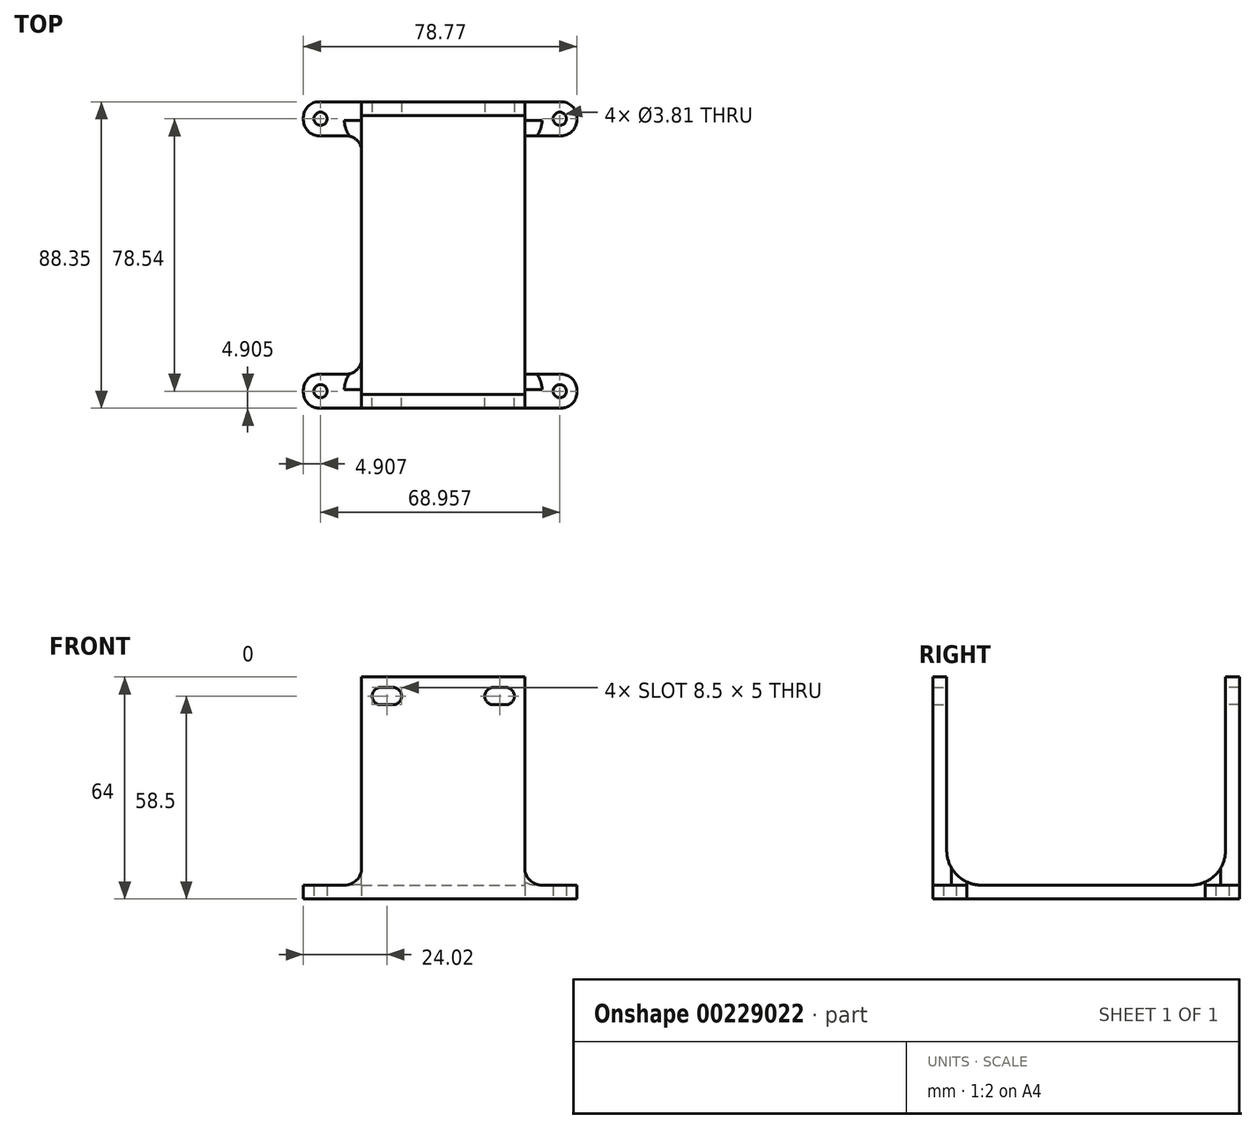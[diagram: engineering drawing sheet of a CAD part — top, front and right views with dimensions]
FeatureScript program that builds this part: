
annotation { "Feature Type Name" : "Feature", "Feature Type Description" : "" }
export const myFeature = defineFeature(function(context is Context, id is Id, definition is map)
    precondition{}
    {
        {
            var Q0;
            Q0=qCreatedBy(makeId("Front.planeOp"),FACE);
            var sketch = newSketch(context, id + "F0", { "sketchPlane" : qUnion([Q0])});
            skLineSegment(sketch, "E0.bottom", {"start": v(0, 0) * mm, "end": v(47, 0) * mm});
            skLineSegment(sketch, "E0.top", {"start": v(0, 64) * mm, "end": v(47, 64) * mm});
            skLineSegment(sketch, "E0.left", {"start": v(0, 0) * mm, "end": v(0, 64) * mm});
            skLineSegment(sketch, "E0.right", {"start": v(47, 0) * mm, "end": v(47, 64) * mm});
            skLineSegment(sketch, "E1", {"start": v(23.5, 64) * mm, "end": v(23.5, 61) * mm, "construction": true});
            skLineSegment(sketch, "E2", {"start": v(23.5, 61) * mm, "end": v(3, 61) * mm, "construction": true});
            skLineSegment(sketch, "E3", {"start": v(3, 61) * mm, "end": v(0, 61) * mm, "construction": true});
            skLineSegment(sketch, "E4", {"start": v(23.5, 61) * mm, "end": v(44, 61) * mm, "construction": true});
            skLineSegment(sketch, "E5", {"start": v(44, 61) * mm, "end": v(47, 61) * mm, "construction": true});
            skLineSegment(sketch, "E6", {"start": v(3, 61) * mm, "end": v(3, 56) * mm, "construction": true});
            skLineSegment(sketch, "E7", {"start": v(44, 61) * mm, "end": v(44, 56) * mm, "construction": true});
            skLineSegment(sketch, "E8", {"start": v(3, 58.5) * mm, "end": v(5.5, 58.5) * mm, "construction": true});
            skLineSegment(sketch, "E9", {"start": v(44, 58.5) * mm, "end": v(41.5, 58.5) * mm, "construction": true});
            skArc(sketch, "E10", {"start": v(5.5, 61) * mm, "mid": v(3, 58.5) * mm, "end": v(5.5, 56) * mm});
            skArc(sketch, "E11", {"start": v(41.5, 61) * mm, "mid": v(44, 58.5) * mm, "end": v(41.5, 56) * mm});
            skLineSegment(sketch, "E12", {"start": v(5.5, 58.5) * mm, "end": v(9, 58.5) * mm, "construction": true});
            skLineSegment(sketch, "E13", {"start": v(41.5, 58.5) * mm, "end": v(38, 58.5) * mm, "construction": true});
            skArc(sketch, "E14", {"start": v(9, 61) * mm, "mid": v(11.5, 58.5) * mm, "end": v(9, 56) * mm});
            skArc(sketch, "E15", {"start": v(38, 61) * mm, "mid": v(35.5, 58.5) * mm, "end": v(38, 56) * mm});
            skLineSegment(sketch, "E16", {"start": v(9, 61) * mm, "end": v(5.5, 61) * mm});
            skLineSegment(sketch, "E17", {"start": v(5.5, 56) * mm, "end": v(9, 56) * mm});
            skLineSegment(sketch, "E18", {"start": v(38, 61) * mm, "end": v(41.5, 61) * mm});
            skLineSegment(sketch, "E19", {"start": v(38, 56) * mm, "end": v(41.5, 56) * mm});
            skSolve(sketch);
        }
        {
            var Q0;
            Q0 = qSketchRegion(id + "F0", true);
            extrude(context, id + "F1", {"entities" : qUnion([Q0]), "depth" : 4 * mm});
        }
        {
            var Q0;
            Q0=makeQuery(id+"F1.opExtrude","SWEPT_FACE",FACE,{"disambiguationData":[OSD([sQuery(id+"F0.wireOp",EDGE,"E0.bottom")])]});
            var sketch = newSketch(context, id + "F2", { "sketchPlane" : qUnion([Q0])});
            skLineSegment(sketch, "E20.bottom", {"start": v(47, 4) * mm, "end": v(0, 4) * mm});
            skLineSegment(sketch, "E20.top", {"start": v(47, -40.18) * mm, "end": v(0, -40.18) * mm});
            skLineSegment(sketch, "E20.left", {"start": v(47, 4) * mm, "end": v(47, -40.18) * mm});
            skLineSegment(sketch, "E20.right", {"start": v(0, 4) * mm, "end": v(0, -40.18) * mm});
            skSolve(sketch);
        }
        {
            var Q0;
            Q0 = qSketchRegion(id + "F2", true);
            extrude(context, id + "F3", {"entities" : qUnion([Q0]), "operationType" : NewBodyOperationType.ADD, "oppositeDirection" : true, "depth" : 4 * mm});
        }
        {
            var Q0;
            Q0=makeQuery(id+"F3.boolean.opBoolean","MERGE",FACE,{"derivedFrom":[makeQuery(id+"F1.opExtrude","SWEPT_FACE",FACE,{"disambiguationData":[OSD([sQuery(id+"F0.wireOp",EDGE,"E0.bottom")])]}),makeQuery(id+"F3.opExtrude","CAP_FACE",FACE,{"disambiguationData":[OSD([sQuery(id+"F2.wireOp",EDGE,"E20.bottom"),sQuery(id+"F2.wireOp",EDGE,"E20.top"),sQuery(id+"F2.wireOp",EDGE,"E20.left"),sQuery(id+"F2.wireOp",EDGE,"E20.right")])],"isStart":true})]});
            var sketch = newSketch(context, id + "F4", { "sketchPlane" : qUnion([Q0])});
            skLineSegment(sketch, "E21.bottom", {"start": v(47, 4) * mm, "end": v(62, 4) * mm});
            skLineSegment(sketch, "E21.top", {"start": v(47, -5.81) * mm, "end": v(62, -5.81) * mm});
            skLineSegment(sketch, "E21.left", {"start": v(47, 4) * mm, "end": v(47, -5.81) * mm});
            skLineSegment(sketch, "E21.right", {"start": v(62, 4) * mm, "end": v(62, -5.81) * mm});
            skCircle(sketch, "E22", {"center": v(57.1, -0.9) * mm, "radius": 1.9 * mm});
            skLineSegment(sketch, "E23", {"start": v(-16.77, 4) * mm, "end": v(-16.77, -5.81) * mm});
            skCircle(sketch, "E24", {"center": v(-11.86, -0.9) * mm, "radius": 1.9 * mm});
            skLineSegment(sketch, "E25", {"start": v(-11.86, -0.9) * mm, "end": v(-11.86, 1) * mm});
            skLineSegment(sketch, "E26", {"start": v(-11.86, 1) * mm, "end": v(-11.86, 4) * mm, "construction": true});
            skLineSegment(sketch, "E27", {"start": v(-11.86, -0.9) * mm, "end": v(-11.86, -2.81) * mm});
            skLineSegment(sketch, "E28", {"start": v(-11.86, -2.81) * mm, "end": v(-11.86, -5.8) * mm, "construction": true});
            skLineSegment(sketch, "E29", {"start": v(-16.77, -5.8) * mm, "end": v(-11.86, -5.8) * mm});
            skLineSegment(sketch, "E30", {"start": v(-11.86, 4) * mm, "end": v(0, 4) * mm});
            skLineSegment(sketch, "E31", {"start": v(-11.86, 4) * mm, "end": v(-16.77, 4) * mm});
            skLineSegment(sketch, "E32", {"start": v(-11.86, -5.8) * mm, "end": v(0.23, -5.8) * mm});
            skLineSegment(sketch, "E33", {"start": v(-16.77, -0.9) * mm, "end": v(-13.77, -0.9) * mm, "construction": true});
            skLineSegment(sketch, "E34", {"start": v(57.1, -0.9) * mm, "end": v(57.1, 1) * mm, "construction": true});
            skLineSegment(sketch, "E35", {"start": v(57.1, 1) * mm, "end": v(57.1, 4) * mm, "construction": true});
            skLineSegment(sketch, "E36", {"start": v(57.1, -0.9) * mm, "end": v(57.1, -2.81) * mm, "construction": true});
            skLineSegment(sketch, "E37", {"start": v(57.1, -2.81) * mm, "end": v(57.1, -5.81) * mm, "construction": true});
            skLineSegment(sketch, "E38", {"start": v(57.1, -0.9) * mm, "end": v(59, -0.9) * mm, "construction": true});
            skLineSegment(sketch, "E39", {"start": v(59, -0.9) * mm, "end": v(62, -0.9) * mm, "construction": true});
            skLineSegment(sketch, "E40", {"start": v(0, 4) * mm, "end": v(1.28, 4) * mm});
            skLineSegment(sketch, "E41", {"start": v(1.28, 3.98) * mm, "end": v(1.28, -5.96) * mm});
            skLineSegment(sketch, "E42", {"start": v(0.23, -5.81) * mm, "end": v(1.28, -5.96) * mm});
            skLineSegment(sketch, "E43", {"start": v(47, 4) * mm, "end": v(45.9, 4) * mm});
            skLineSegment(sketch, "E44", {"start": v(45.9, 3.85) * mm, "end": v(45.9, -5.8) * mm});
            skLineSegment(sketch, "E45", {"start": v(45.9, -5.8) * mm, "end": v(47, -5.81) * mm});
            skSolve(sketch);
        }
        {
            var Q0;
            Q0=makeQuery(id+"F4.imprint","IMPRINT",FACE,{"disambiguationData":[TD([[makeQuery(id+"F4.imprint","IMPRINT",EDGE,{"derivedFrom":sQuery(id+"F4.wireOp",EDGE,"E23")}),1.0]])]});
            var Q1;
            {var subQ6=sQuery(id+"F4.wireOp",EDGE,"E21.left");Q1=makeQuery(id+"F4.imprint","IMPRINT",FACE,{"disambiguationData":[TD([[makeQuery(id+"F4.imprint","IMPRINT",EDGE,{"derivedFrom":subQ6}),-1.0]])]});}
            var Q2;
            Q2=makeQuery(id+"F4.imprint","IMPRINT",FACE,{"disambiguationData":[TD([[makeQuery(id+"F4.imprint","IMPRINT",EDGE,{"derivedFrom":sQuery(id+"F4.wireOp",EDGE,"E21.bottom")}),-1.0]])]});
            extrude(context, id + "F5", {"entities" : qUnion([Q0, Q1, Q2]), "operationType" : NewBodyOperationType.ADD, "oppositeDirection" : true, "depth" : 4 * mm});
        }
        {
            var Q0;
            Q0=makeQuery(id+"F3.boolean.opBoolean","INTERSECT",EDGE,{"derivedFrom":[makeQuery(id+"F1.opExtrude","CAP_FACE",FACE,{"disambiguationData":[OSD([sQuery(id+"F0.wireOp",EDGE,"E0.bottom"),sQuery(id+"F0.wireOp",EDGE,"E0.top"),sQuery(id+"F0.wireOp",EDGE,"E0.left"),sQuery(id+"F0.wireOp",EDGE,"E0.right"),sQuery(id+"F0.wireOp",EDGE,"E10"),sQuery(id+"F0.wireOp",EDGE,"E11"),sQuery(id+"F0.wireOp",EDGE,"E14"),sQuery(id+"F0.wireOp",EDGE,"E15"),sQuery(id+"F0.wireOp",EDGE,"E16"),sQuery(id+"F0.wireOp",EDGE,"E17"),sQuery(id+"F0.wireOp",EDGE,"E18"),sQuery(id+"F0.wireOp",EDGE,"E19")])],"isStart":true}),makeQuery(id+"F3.opExtrude","CAP_FACE",FACE,{"disambiguationData":[OSD([sQuery(id+"F2.wireOp",EDGE,"E20.bottom"),sQuery(id+"F2.wireOp",EDGE,"E20.top"),sQuery(id+"F2.wireOp",EDGE,"E20.left"),sQuery(id+"F2.wireOp",EDGE,"E20.right")])],"isStart":false})]});
            fillet(context, id + "F6", {"entities" : qUnion([Q0]), "radius" : 10 * mm, "tangentPropagation" : true, "allowEdgeOverflow" : false});
        }
        {
            var Q0;
            {var subQ0=sQuery(id+"F2.wireOp",EDGE,"E20.right");var subQ1=sQuery(id+"F0.wireOp",EDGE,"E0.left");Q0=makeQuery(id+"F5.boolean.opBoolean","INTERSECT",EDGE,{"derivedFrom":[makeQuery(id+"F3.boolean.opBoolean","MERGE",FACE,{"derivedFrom":[makeQuery(id+"F1.opExtrude","SWEPT_FACE",FACE,{"disambiguationData":[OSD([subQ1])]}),makeQuery(id+"F3.opExtrude","SWEPT_FACE",FACE,{"disambiguationData":[OSD([subQ0])]})]}),makeQuery(id+"F5.opExtrude","CAP_FACE",FACE,{"disambiguationData":[OSD([sQuery(id+"F0.wireOp",EDGE,"E0.bottom"),subQ1,sQuery(id+"F0.wireOp",EDGE,"E0.right"),sQuery(id+"F2.wireOp",EDGE,"E20.top"),sQuery(id+"F2.wireOp",EDGE,"E20.left"),subQ0,sQuery(id+"F4.wireOp",EDGE,"E21.bottom"),sQuery(id+"F4.wireOp",EDGE,"E21.top"),sQuery(id+"F4.wireOp",EDGE,"E21.right"),sQuery(id+"F4.wireOp",EDGE,"E22"),sQuery(id+"F4.wireOp",EDGE,"E23"),sQuery(id+"F4.wireOp",EDGE,"E24"),sQuery(id+"F4.wireOp",EDGE,"E29"),sQuery(id+"F4.wireOp",EDGE,"E30"),sQuery(id+"F4.wireOp",EDGE,"E31"),sQuery(id+"F4.wireOp",EDGE,"E32"),sQuery(id+"F4.wireOp",EDGE,"E40"),sQuery(id+"F4.wireOp",EDGE,"E42"),sQuery(id+"F4.wireOp",EDGE,"E43")])],"isStart":false})]});}
            var Q1;
            {var subQ0=sQuery(id+"F2.wireOp",EDGE,"E20.left");var subQ1=sQuery(id+"F0.wireOp",EDGE,"E0.right");Q1=makeQuery(id+"F5.boolean.opBoolean","INTERSECT",EDGE,{"derivedFrom":[makeQuery(id+"F3.boolean.opBoolean","MERGE",FACE,{"derivedFrom":[makeQuery(id+"F1.opExtrude","SWEPT_FACE",FACE,{"disambiguationData":[OSD([subQ1])]}),makeQuery(id+"F3.opExtrude","SWEPT_FACE",FACE,{"disambiguationData":[OSD([subQ0])]})]}),makeQuery(id+"F5.opExtrude","CAP_FACE",FACE,{"disambiguationData":[OSD([sQuery(id+"F0.wireOp",EDGE,"E0.bottom"),sQuery(id+"F0.wireOp",EDGE,"E0.left"),subQ1,sQuery(id+"F2.wireOp",EDGE,"E20.top"),subQ0,sQuery(id+"F2.wireOp",EDGE,"E20.right"),sQuery(id+"F4.wireOp",EDGE,"E21.bottom"),sQuery(id+"F4.wireOp",EDGE,"E21.top"),sQuery(id+"F4.wireOp",EDGE,"E21.right"),sQuery(id+"F4.wireOp",EDGE,"E22"),sQuery(id+"F4.wireOp",EDGE,"E23"),sQuery(id+"F4.wireOp",EDGE,"E24"),sQuery(id+"F4.wireOp",EDGE,"E29"),sQuery(id+"F4.wireOp",EDGE,"E30"),sQuery(id+"F4.wireOp",EDGE,"E31"),sQuery(id+"F4.wireOp",EDGE,"E32"),sQuery(id+"F4.wireOp",EDGE,"E40"),sQuery(id+"F4.wireOp",EDGE,"E42"),sQuery(id+"F4.wireOp",EDGE,"E43")])],"isStart":false})]});}
            fillet(context, id + "F7", {"entities" : qUnion([Q0, Q1]), "radius" : 5 * mm, "tangentPropagation" : true, "allowEdgeOverflow" : false});
        }
        {
            var Q0;
            Q0=makeQuery(id+"F5.opExtrude","SWEPT_EDGE",EDGE,{"disambiguationData":[OSD([sQuery(id+"F4.wireOp",EDGE,"E23"),sQuery(id+"F4.wireOp",EDGE,"E31")])]});
            var Q1;
            Q1=makeQuery(id+"F5.opExtrude","SWEPT_EDGE",EDGE,{"disambiguationData":[OSD([sQuery(id+"F4.wireOp",EDGE,"E23"),sQuery(id+"F4.wireOp",EDGE,"E29")])]});
            var Q2;
            Q2=makeQuery(id+"F5.opExtrude","SWEPT_EDGE",EDGE,{"disambiguationData":[OSD([sQuery(id+"F4.wireOp",EDGE,"E21.bottom"),sQuery(id+"F4.wireOp",EDGE,"E21.right")])]});
            var Q3;
            Q3=makeQuery(id+"F5.opExtrude","SWEPT_EDGE",EDGE,{"disambiguationData":[OSD([sQuery(id+"F4.wireOp",EDGE,"E21.top"),sQuery(id+"F4.wireOp",EDGE,"E21.right")])]});
            var Q4;
            Q4=makeQuery(id+"F5.opExtrude","SWEPT_EDGE",EDGE,{"disambiguationData":[OSD([sQuery(id+"F0.wireOp",EDGE,"E0.bottom"),sQuery(id+"F0.wireOp",EDGE,"E0.right"),sQuery(id+"F2.wireOp",EDGE,"E20.left"),sQuery(id+"F4.wireOp",EDGE,"E21.top"),sQuery(id+"F4.wireOp",EDGE,"E21.left")])]});
            var Q5;
            {var subQ0=sQuery(id+"F2.wireOp",EDGE,"E20.right");var subQ1=sQuery(id+"F0.wireOp",EDGE,"E0.left");var subQ2=sQuery(id+"F0.wireOp",EDGE,"E0.bottom");Q5=makeQuery(id+"F7.opFillet","TWEAK_EDGE",EDGE,{"derivedFrom":[makeQuery(id+"F6.opFillet","TWEAK_VERTEX",VERTEX,{"derivedFrom":[makeQuery(id+"F3.boolean.opBoolean","INTERSECT",VERTEX,{"disambiguationData":[OD(0.0)],"derivedFrom":[makeQuery(id+"F1.opExtrude","CAP_FACE",FACE,{"disambiguationData":[OSD([subQ2,sQuery(id+"F0.wireOp",EDGE,"E0.top"),subQ1,sQuery(id+"F0.wireOp",EDGE,"E0.right"),sQuery(id+"F0.wireOp",EDGE,"E10"),sQuery(id+"F0.wireOp",EDGE,"E11"),sQuery(id+"F0.wireOp",EDGE,"E14"),sQuery(id+"F0.wireOp",EDGE,"E15"),sQuery(id+"F0.wireOp",EDGE,"E16"),sQuery(id+"F0.wireOp",EDGE,"E17"),sQuery(id+"F0.wireOp",EDGE,"E18"),sQuery(id+"F0.wireOp",EDGE,"E19")])],"isStart":true}),makeQuery(id+"F3.opExtrude","CAP_FACE",FACE,{"disambiguationData":[OSD([sQuery(id+"F2.wireOp",EDGE,"E20.bottom"),sQuery(id+"F2.wireOp",EDGE,"E20.top"),sQuery(id+"F2.wireOp",EDGE,"E20.left"),subQ0])],"isStart":false})]}),makeQuery(id+"F5.opExtrude","CAP_VERTEX",VERTEX,{"disambiguationData":[OSD([subQ2,subQ1,subQ0,sQuery(id+"F4.wireOp",EDGE,"E42")])],"isStart":false})]})]});}
            var Q6;
            Q6=makeQuery(id+"F5.opExtrude","SWEPT_EDGE",EDGE,{"disambiguationData":[OSD([sQuery(id+"F0.wireOp",EDGE,"E0.bottom"),sQuery(id+"F0.wireOp",EDGE,"E0.left"),sQuery(id+"F2.wireOp",EDGE,"E20.right"),sQuery(id+"F4.wireOp",EDGE,"E42")])]});
            fillet(context, id + "F8", {"entities" : qUnion([Q0, Q1, Q2, Q3, Q4, Q5, Q6]), "radius" : 4.5 * mm, "tangentPropagation" : true, "allowEdgeOverflow" : false});
        }
        {
            var Q0;
            Q0=makeQuery(id+"F1.opExtrude","SWEPT_BODY",BODY,{"disambiguationData":[OSD([sQuery(id+"F0.wireOp",EDGE,"E0.bottom"),sQuery(id+"F0.wireOp",EDGE,"E0.top"),sQuery(id+"F0.wireOp",EDGE,"E0.left"),sQuery(id+"F0.wireOp",EDGE,"E0.right"),sQuery(id+"F0.wireOp",EDGE,"E10"),sQuery(id+"F0.wireOp",EDGE,"E11"),sQuery(id+"F0.wireOp",EDGE,"E14"),sQuery(id+"F0.wireOp",EDGE,"E15"),sQuery(id+"F0.wireOp",EDGE,"E16"),sQuery(id+"F0.wireOp",EDGE,"E17"),sQuery(id+"F0.wireOp",EDGE,"E18"),sQuery(id+"F0.wireOp",EDGE,"E19")])]});
            var Q1;
            Q1=makeQuery(id+"F3.opExtrude","SWEPT_FACE",FACE,{"disambiguationData":[OSD([sQuery(id+"F2.wireOp",EDGE,"E20.top")])]});
            mirror(context, id + "F9", {"operationType" : NewBodyOperationType.ADD, "entities" : qUnion([Q0]), "mirrorPlane" : qUnion([Q1])});
        }
    });
